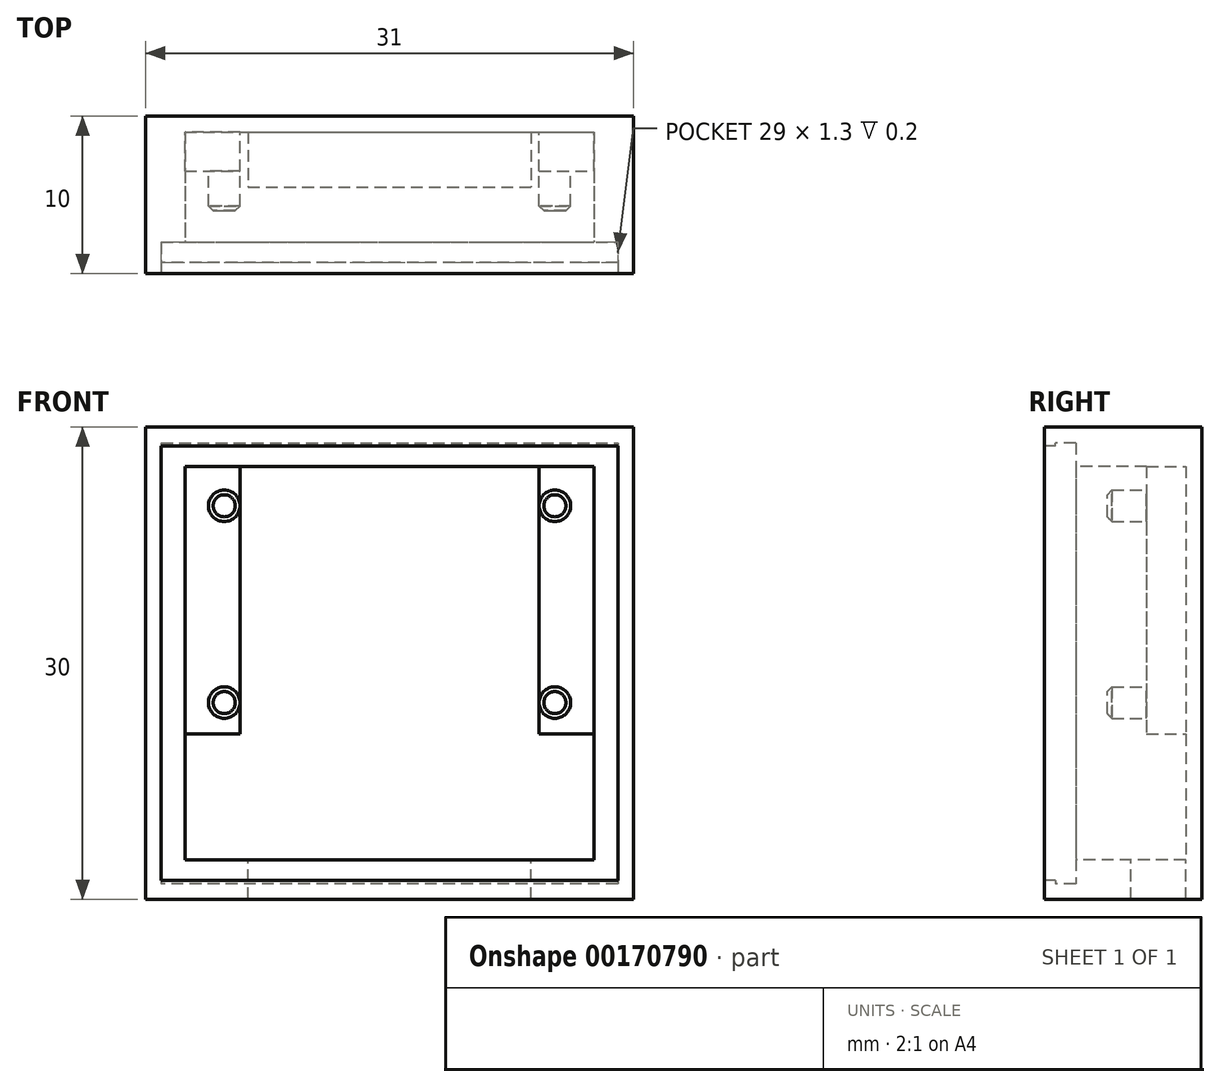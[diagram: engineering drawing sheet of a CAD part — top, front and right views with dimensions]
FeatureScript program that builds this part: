
annotation { "Feature Type Name" : "Feature", "Feature Type Description" : "" }
export const myFeature = defineFeature(function(context is Context, id is Id, definition is map)
    precondition{}
    {
        {
            var Q0;
            Q0=qCreatedBy(makeId("Front.planeOp"),FACE);
            var sketch = newSketch(context, id + "F0", { "sketchPlane" : qUnion([Q0])});
            skLineSegment(sketch, "E0.bottom", {"start": v(-15.5, 17.5) * mm, "end": v(15.5, 17.5) * mm});
            skLineSegment(sketch, "E0.top", {"start": v(-15.5, -12.5) * mm, "end": v(15.5, -12.5) * mm});
            skLineSegment(sketch, "E0.left", {"start": v(-15.5, 17.5) * mm, "end": v(-15.5, -12.5) * mm});
            skLineSegment(sketch, "E0.right", {"start": v(15.5, 17.5) * mm, "end": v(15.5, -12.5) * mm});
            skLineSegment(sketch, "E1", {"start": v(0, 17.5) * mm, "end": v(0, -12.5) * mm});
            skLineSegment(sketch, "E2", {"start": v(-15.5, 2.5) * mm, "end": v(15.5, 2.5) * mm});
            skLineSegment(sketch, "E3.bottom", {"start": v(-12.5, 14.5) * mm, "end": v(12.5, 14.5) * mm, "construction": true});
            skLineSegment(sketch, "E3.top", {"start": v(-12.5, -9.5) * mm, "end": v(12.5, -9.5) * mm, "construction": true});
            skLineSegment(sketch, "E3.left", {"start": v(-12.5, 14.5) * mm, "end": v(-12.5, -9.5) * mm, "construction": true});
            skLineSegment(sketch, "E3.right", {"start": v(12.5, 14.5) * mm, "end": v(12.5, -9.5) * mm, "construction": true});
            skLineSegment(sketch, "E4", {"start": v(-12.5, 2.5) * mm, "end": v(12.5, 2.5) * mm, "construction": true});
            skLineSegment(sketch, "E5", {"start": v(0, 14.5) * mm, "end": v(0, -9.5) * mm, "construction": true});
            skLineSegment(sketch, "E6", {"start": v(-12.5, 0) * mm, "end": v(12.5, 0) * mm, "construction": true});
            skSolve(sketch);
        }
        {
            var Q0;
            Q0 = qSketchRegion(id + "F0", true);
            extrude(context, id + "F1", {"entities" : qUnion([Q0]), "depth" : 10 * mm});
        }
        {
            var Q0;
            Q0=makeQuery(id+"F1.opExtrude","CAP_FACE",FACE,{"disambiguationData":[OSD([sQuery(id+"F0.wireOp",EDGE,"E0.bottom"),sQuery(id+"F0.wireOp",EDGE,"E0.top"),sQuery(id+"F0.wireOp",EDGE,"E0.left"),sQuery(id+"F0.wireOp",EDGE,"E0.right")])],"isStart":false});
            var sketch = newSketch(context, id + "F2", { "sketchPlane" : qUnion([Q0])});
            skLineSegment(sketch, "E7.bottom", {"start": v(-14.5, 16.5) * mm, "end": v(14.5, 16.5) * mm});
            skLineSegment(sketch, "E7.top", {"start": v(-14.5, -11.5) * mm, "end": v(14.5, -11.5) * mm});
            skLineSegment(sketch, "E7.left", {"start": v(-14.5, 16.5) * mm, "end": v(-14.5, -11.5) * mm});
            skLineSegment(sketch, "E7.right", {"start": v(14.5, 16.5) * mm, "end": v(14.5, -11.5) * mm});
            skSolve(sketch);
        }
        {
            var Q0;
            Q0 = qSketchRegion(id + "F2", true);
            extrude(context, id + "F3", {"entities" : qUnion([Q0]), "operationType" : NewBodyOperationType.REMOVE, "oppositeDirection" : true, "depth" : 2 * mm});
        }
        {
            var Q0;
            Q0=makeQuery(id+"F3.boolean.opBoolean","COPY",FACE,{"derivedFrom":makeQuery(id+"F3.opExtrude","CAP_FACE",FACE,{"disambiguationData":[OSD([sQuery(id+"F2.wireOp",EDGE,"E7.bottom"),sQuery(id+"F2.wireOp",EDGE,"E7.top"),sQuery(id+"F2.wireOp",EDGE,"E7.left"),sQuery(id+"F2.wireOp",EDGE,"E7.right")])],"isStart":false})});
            var sketch = newSketch(context, id + "F4", { "sketchPlane" : qUnion([Q0])});
            skLineSegment(sketch, "E8.bottom", {"start": v(-13, 15) * mm, "end": v(13, 15) * mm});
            skLineSegment(sketch, "E8.top", {"start": v(-13, -10) * mm, "end": v(13, -10) * mm});
            skLineSegment(sketch, "E8.left", {"start": v(-13, 15) * mm, "end": v(-13, -10) * mm});
            skLineSegment(sketch, "E8.right", {"start": v(13, 15) * mm, "end": v(13, -10) * mm});
            skSolve(sketch);
        }
        {
            var Q0;
            Q0 = qSketchRegion(id + "F4", true);
            extrude(context, id + "F5", {"entities" : qUnion([Q0]), "operationType" : NewBodyOperationType.REMOVE, "oppositeDirection" : true, "depth" : 7 * mm});
        }
        {
            var Q0;
            Q0=makeQuery(id+"F5.boolean.opBoolean","COPY",FACE,{"derivedFrom":makeQuery(id+"F5.opExtrude","CAP_FACE",FACE,{"disambiguationData":[OSD([sQuery(id+"F4.wireOp",EDGE,"E8.bottom"),sQuery(id+"F4.wireOp",EDGE,"E8.top"),sQuery(id+"F4.wireOp",EDGE,"E8.left"),sQuery(id+"F4.wireOp",EDGE,"E8.right")])],"isStart":false})});
            var sketch = newSketch(context, id + "F6", { "sketchPlane" : qUnion([Q0])});
            skLineSegment(sketch, "E9.bottom", {"start": v(-9.5, 15) * mm, "end": v(-13, 15) * mm});
            skLineSegment(sketch, "E9.top", {"start": v(-9.5, -2) * mm, "end": v(-13, -2) * mm});
            skLineSegment(sketch, "E9.left", {"start": v(-9.5, 15) * mm, "end": v(-9.5, -2) * mm});
            skLineSegment(sketch, "E9.right", {"start": v(-13, 15) * mm, "end": v(-13, -2) * mm});
            skLineSegment(sketch, "E10.MirrorCS", {"start": v(9.5, 15) * mm, "end": v(9.5, -2) * mm});
            skLineSegment(sketch, "E11.MirrorCS", {"start": v(9.5, 15) * mm, "end": v(13, 15) * mm});
            skLineSegment(sketch, "E12.MirrorCS", {"start": v(13, 15) * mm, "end": v(13, -2) * mm});
            skLineSegment(sketch, "E13.MirrorCS", {"start": v(9.5, -2) * mm, "end": v(13, -2) * mm});
            skSolve(sketch);
        }
        {
            var Q0;
            Q0 = qSketchRegion(id + "F6", true);
            extrude(context, id + "F7", {"entities" : qUnion([Q0]), "operationType" : NewBodyOperationType.ADD, "depth" : 2.5 * mm});
        }
        {
            var Q0;
            Q0=makeQuery(id+"F7.opExtrude","CAP_FACE",FACE,{"disambiguationData":[OSD([sQuery(id+"F6.wireOp",EDGE,"E9.bottom"),sQuery(id+"F6.wireOp",EDGE,"E9.top"),sQuery(id+"F6.wireOp",EDGE,"E9.left"),sQuery(id+"F6.wireOp",EDGE,"E9.right")])],"isStart":false});
            var sketch = newSketch(context, id + "F8", { "sketchPlane" : qUnion([Q0])});
            skCircle(sketch, "E14", {"center": v(-10.5, 12.5) * mm, "radius": 1 * mm});
            skCircle(sketch, "E15", {"center": v(-10.5, 0) * mm, "radius": 1 * mm});
            skCircle(sketch, "E16.MirrorC", {"center": v(10.5, 12.5) * mm, "radius": 1 * mm});
            skCircle(sketch, "E17.MirrorC", {"center": v(10.5, 0) * mm, "radius": 1 * mm});
            skSolve(sketch);
        }
        {
            var Q0;
            Q0 = qSketchRegion(id + "F8", true);
            extrude(context, id + "F9", {"entities" : qUnion([Q0]), "operationType" : NewBodyOperationType.ADD, "depth" : 2.5 * mm});
        }
        {
            var Q0;
            Q0=makeQuery(id+"F5.boolean.opBoolean","COPY",FACE,{"derivedFrom":makeQuery(id+"F5.opExtrude","SWEPT_FACE",FACE,{"disambiguationData":[OSD([sQuery(id+"F4.wireOp",EDGE,"E8.top")])]})});
            var sketch = newSketch(context, id + "F10", { "sketchPlane" : qUnion([Q0])});
            skLineSegment(sketch, "E18.bottom", {"start": v(-9, -1) * mm, "end": v(9, -1) * mm});
            skLineSegment(sketch, "E18.top", {"start": v(-9, -4.5) * mm, "end": v(9, -4.5) * mm});
            skLineSegment(sketch, "E18.left", {"start": v(-9, -1) * mm, "end": v(-9, -4.5) * mm});
            skLineSegment(sketch, "E18.right", {"start": v(9, -1) * mm, "end": v(9, -4.5) * mm});
            skSolve(sketch);
        }
        {
            var Q0;
            Q0 = qSketchRegion(id + "F10", true);
            extrude(context, id + "F11", {"entities" : qUnion([Q0]), "operationType" : NewBodyOperationType.REMOVE, "oppositeDirection" : true, "depth" : 25 * mm});
        }
        {
            var Q0;
            Q0=makeQuery(id+"F9.opExtrude","CAP_EDGE",EDGE,{"disambiguationData":[OSD([sQuery(id+"F8.wireOp",EDGE,"E14")])],"isStart":false});
            var Q1;
            Q1=makeQuery(id+"F9.opExtrude","CAP_EDGE",EDGE,{"disambiguationData":[OSD([sQuery(id+"F8.wireOp",EDGE,"E15")])],"isStart":false});
            var Q2;
            Q2=makeQuery(id+"F9.opExtrude","CAP_EDGE",EDGE,{"disambiguationData":[OSD([sQuery(id+"F8.wireOp",EDGE,"E16.MirrorC")])],"isStart":false});
            var Q3;
            Q3=makeQuery(id+"F9.opExtrude","CAP_EDGE",EDGE,{"disambiguationData":[OSD([sQuery(id+"F8.wireOp",EDGE,"E17.MirrorC")])],"isStart":false});
            chamfer(context, id + "F12", {"entities" : qUnion([Q0, Q1, Q2, Q3]), "width" : .3 * mm, "tangentPropagation" : true});
        }
        {
            var Q0;
            Q0=makeQuery(id+"F3.boolean.opBoolean","COPY",FACE,{"derivedFrom":makeQuery(id+"F3.opExtrude","SWEPT_FACE",FACE,{"disambiguationData":[OSD([sQuery(id+"F2.wireOp",EDGE,"E7.bottom")])]})});
            var sketch = newSketch(context, id + "F13", { "sketchPlane" : qUnion([Q0])});
            skLineSegment(sketch, "E19.bottom", {"start": v(-14.5, 10) * mm, "end": v(14.5, 10) * mm});
            skLineSegment(sketch, "E19.top", {"start": v(-14.5, 9.3) * mm, "end": v(14.5, 9.3) * mm});
            skLineSegment(sketch, "E19.left", {"start": v(-14.5, 10) * mm, "end": v(-14.5, 9.3) * mm});
            skLineSegment(sketch, "E19.right", {"start": v(14.5, 10) * mm, "end": v(14.5, 9.3) * mm});
            skSolve(sketch);
        }
        {
            var Q0;
            Q0 = qSketchRegion(id + "F13", true);
            extrude(context, id + "F14", {"entities" : qUnion([Q0]), "operationType" : NewBodyOperationType.ADD, "depth" : 0.2 * mm});
        }
        {
            var Q0;
            Q0=makeQuery(id+"F3.boolean.opBoolean","COPY",FACE,{"derivedFrom":makeQuery(id+"F3.opExtrude","SWEPT_FACE",FACE,{"disambiguationData":[OSD([sQuery(id+"F2.wireOp",EDGE,"E7.top")])]})});
            var sketch = newSketch(context, id + "F15", { "sketchPlane" : qUnion([Q0])});
            skLineSegment(sketch, "E20.bottom", {"start": v(14.5, -10) * mm, "end": v(-14.5, -10) * mm});
            skLineSegment(sketch, "E20.top", {"start": v(14.5, -9.3) * mm, "end": v(-14.5, -9.3) * mm});
            skLineSegment(sketch, "E20.left", {"start": v(14.5, -10) * mm, "end": v(14.5, -9.3) * mm});
            skLineSegment(sketch, "E20.right", {"start": v(-14.5, -10) * mm, "end": v(-14.5, -9.3) * mm});
            skSolve(sketch);
        }
        {
            var Q0;
            Q0 = qSketchRegion(id + "F15", true);
            extrude(context, id + "F16", {"entities" : qUnion([Q0]), "operationType" : NewBodyOperationType.ADD, "depth" : 0.2 * mm});
        }
    });
